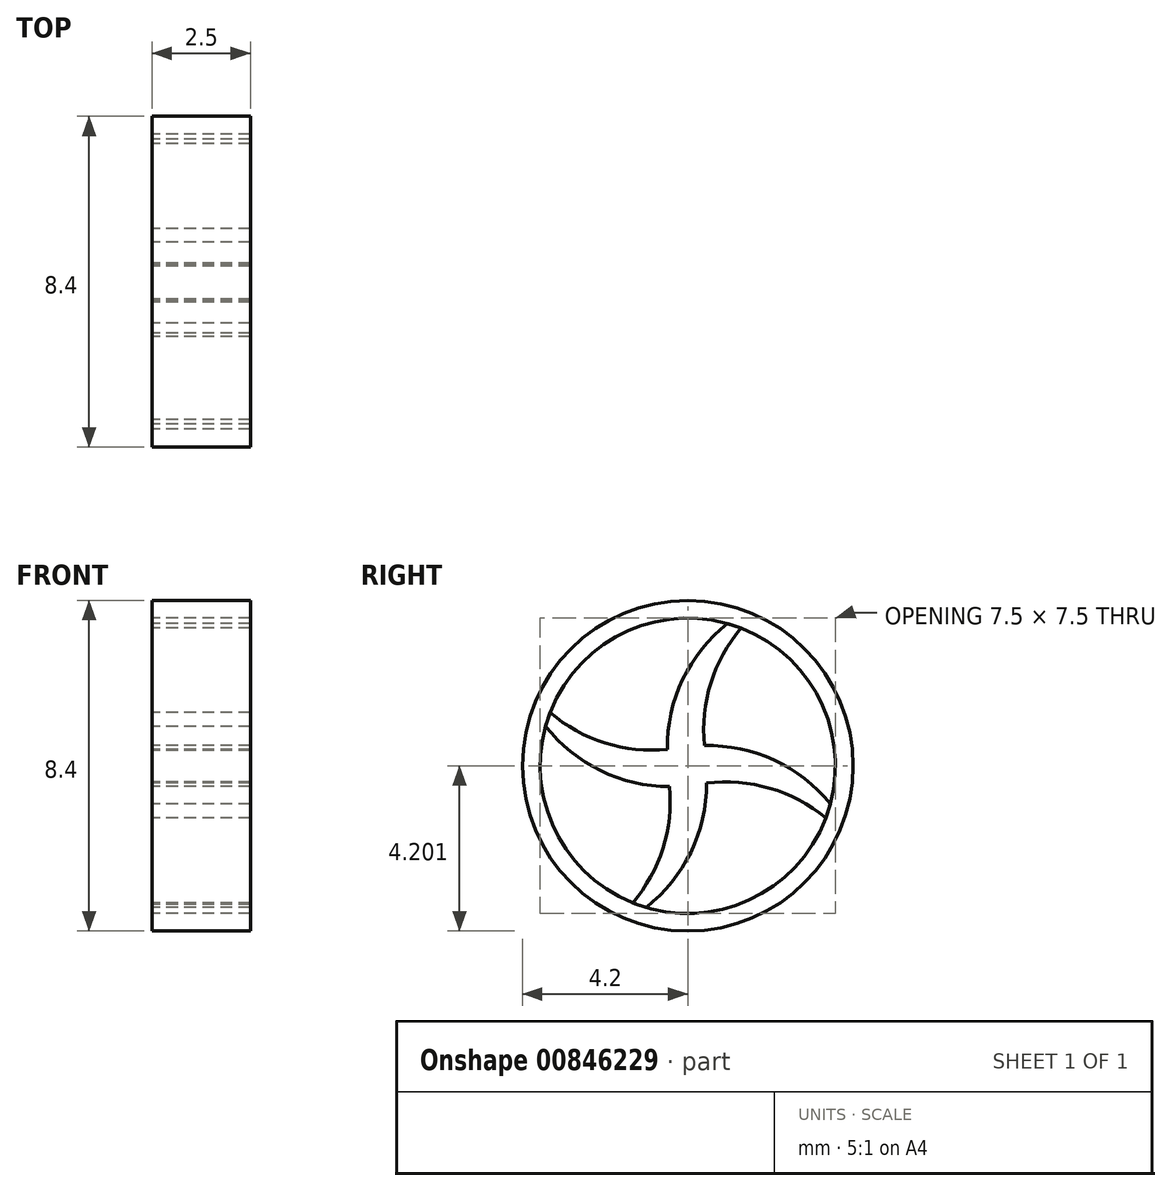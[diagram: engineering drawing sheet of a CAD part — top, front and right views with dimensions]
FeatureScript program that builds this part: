
annotation { "Feature Type Name" : "Feature", "Feature Type Description" : "" }
export const myFeature = defineFeature(function(context is Context, id is Id, definition is map)
    precondition{}
    {
        {
            var Q0;
            Q0=qCreatedBy(makeId("Right.planeOp"),FACE);
            var sketch = newSketch(context, id + "F0", { "sketchPlane" : qUnion([Q0])});
            skCircle(sketch, "E0", {"center": v(0, 0) * mm, "radius": 4.2 * mm});
            skCircle(sketch, "E1", {"center": v(0, 0) * mm, "radius": 3.75 * mm});
            skArc(sketch, "E2", {"start": v(-3.5, 1.35) * mm, "mid": v(-1.85, 0.5) * mm, "end": v(0, 0.5) * mm});
            skArc(sketch, "E3", {"start": v(-3.61, 1) * mm, "mid": v(-2, -0.22) * mm, "end": v(0, -0.5) * mm});
            skArc(sketch, "E4", {"start": v(1.35, 3.5) * mm, "mid": v(0.51, 1.85) * mm, "end": v(0.5, 0) * mm});
            skArc(sketch, "E5", {"start": v(1, 3.61) * mm, "mid": v(-0.22, 2) * mm, "end": v(-0.5, 0) * mm});
            skArc(sketch, "E6", {"start": v(3.55, -1.36) * mm, "mid": v(1.9, -0.52) * mm, "end": v(0.05, -0.51) * mm});
            skArc(sketch, "E7", {"start": v(3.67, -1.02) * mm, "mid": v(2.06, 0.2) * mm, "end": v(0.05, 0.49) * mm});
            skArc(sketch, "E8", {"start": v(-1.4, -3.48) * mm, "mid": v(-0.56, -1.84) * mm, "end": v(-0.55, 0.01) * mm});
            skArc(sketch, "E9", {"start": v(-1.06, -3.6) * mm, "mid": v(0.17, -1.99) * mm, "end": v(0.45, 0.01) * mm});
            skLineSegment(sketch, "E10", {"start": v(1, 3.61) * mm, "end": v(1.35, 3.5) * mm});
            skLineSegment(sketch, "E11", {"start": v(-3.5, 1.35) * mm, "end": v(-3.61, 1) * mm});
            skLineSegment(sketch, "E12", {"start": v(3.62, -0.97) * mm, "end": v(3.5, -1.33) * mm});
            skLineSegment(sketch, "E13", {"start": v(-1.4, -3.48) * mm, "end": v(-1.06, -3.6) * mm});
            skSolve(sketch);
        }
        {
            var Q0;
            Q0=makeQuery(id+"F0.imprint","IMPRINT",FACE,{"disambiguationData":[TD([[makeQuery(id+"F0.imprint","IMPRINT",EDGE,{"derivedFrom":sQuery(id+"F0.wireOp",EDGE,"E0")}),1.0]])]});
            var Q1;
            {var subQ21=sQuery(id+"F0.wireOp",EDGE,"E11");Q1=makeQuery(id+"F0.imprint","IMPRINT",FACE,{"disambiguationData":[TD([[makeQuery(id+"F0.imprint","IMPRINT",EDGE,{"derivedFrom":subQ21}),1.0]])]});}
            extrude(context, id + "F1", {"entities" : qUnion([Q0, Q1]), "endBound" : BoundingType.SYMMETRIC, "depth" : 2.5 * mm, "offsetDistance" : 25 * mm});
        }
    });
